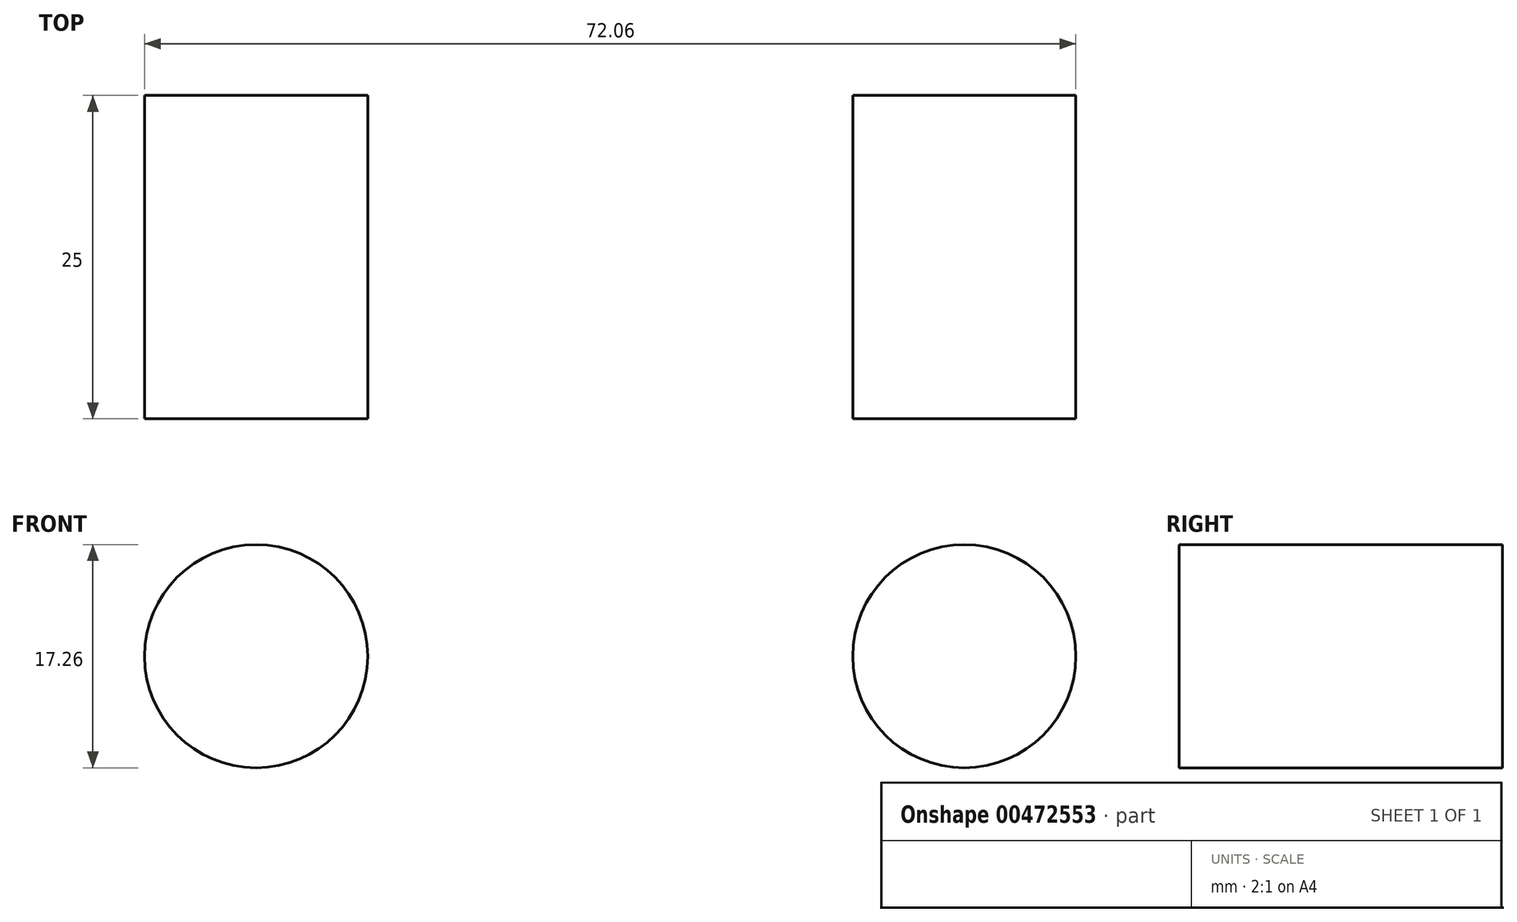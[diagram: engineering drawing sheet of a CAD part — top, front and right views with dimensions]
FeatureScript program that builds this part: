
annotation { "Feature Type Name" : "Feature", "Feature Type Description" : "" }
export const myFeature = defineFeature(function(context is Context, id is Id, definition is map)
    precondition{}
    {
        {
            var Q0;
            Q0=qCreatedBy(makeId("Front.planeOp"),FACE);
            var sketch = newSketch(context, id + "F0", { "sketchPlane" : qUnion([Q0])});
            skCircle(sketch, "E0", {"center": v(-41.05, 20.47) * mm, "radius": 8.63 * mm});
            skCircle(sketch, "E1", {"center": v(13.75, 20.47) * mm, "radius": 8.63 * mm});
            skLineSegment(sketch, "E2", {"start": v(-54.8, 11.84) * mm, "end": v(36.85, 11.84) * mm, "construction": true});
            skSolve(sketch);
        }
        {
            var Q0;
            Q0=makeQuery(id+"F0.imprint","IMPRINT",FACE,{"disambiguationData":[TD([[makeQuery(id+"F0.imprint","IMPRINT",EDGE,{"derivedFrom":sQuery(id+"F0.wireOp",EDGE,"E0")}),1.0]])]});
            var Q1;
            Q1=makeQuery(id+"F0.imprint","IMPRINT",FACE,{"disambiguationData":[TD([[makeQuery(id+"F0.imprint","IMPRINT",EDGE,{"derivedFrom":sQuery(id+"F0.wireOp",EDGE,"E1")}),1.0]])]});
            extrude(context, id + "F1", {"entities" : qUnion([Q0, Q1]), "depth" : 25 * mm});
        }
    });
